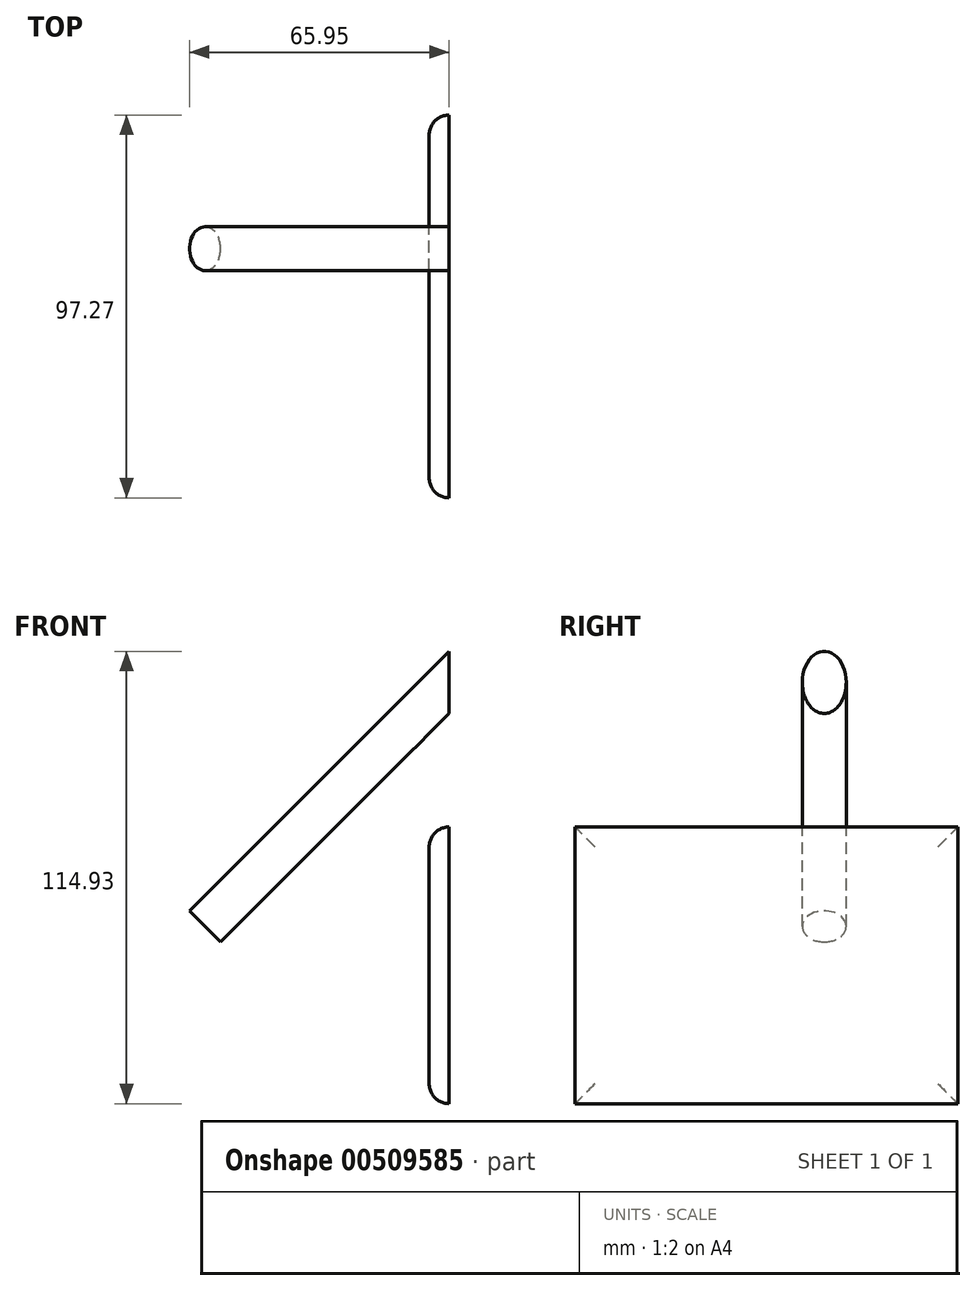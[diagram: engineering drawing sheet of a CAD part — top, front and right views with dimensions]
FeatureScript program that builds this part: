
annotation { "Feature Type Name" : "Feature", "Feature Type Description" : "" }
export const myFeature = defineFeature(function(context is Context, id is Id, definition is map)
    precondition{}
    {
        {
            var Q0;
            Q0=qCreatedBy(makeId("Right.planeOp"),FACE);
            var sketch = newSketch(context, id + "F0", { "sketchPlane" : qUnion([Q0])});
            skLineSegment(sketch, "E0.bottom", {"start": v(-42.41, 32.52) * mm, "end": v(54.86, 32.52) * mm});
            skLineSegment(sketch, "E0.top", {"start": v(-42.41, -37.79) * mm, "end": v(54.86, -37.79) * mm});
            skLineSegment(sketch, "E0.left", {"start": v(-42.41, 32.52) * mm, "end": v(-42.41, -37.79) * mm});
            skLineSegment(sketch, "E0.right", {"start": v(54.86, 32.52) * mm, "end": v(54.86, -37.79) * mm});
            skSolve(sketch);
        }
        {
            var Q0;
            Q0=makeQuery(id+"F0.imprint","IMPRINT",FACE,{"disambiguationData":[TD([[makeQuery(id+"F0.imprint","IMPRINT",EDGE,{"derivedFrom":sQuery(id+"F0.wireOp",EDGE,"E0.bottom")}),-1.0]])]});
            extrude(context, id + "F1", {"entities" : qUnion([Q0]), "oppositeDirection" : true, "depth" : 5.08 * mm});
        }
        {
            var Q0;
            Q0=makeQuery(id+"F1.opExtrude","CAP_FACE",FACE,{"disambiguationData":[OSD([sQuery(id+"F0.wireOp",EDGE,"E0.bottom"),sQuery(id+"F0.wireOp",EDGE,"E0.top"),sQuery(id+"F0.wireOp",EDGE,"E0.left"),sQuery(id+"F0.wireOp",EDGE,"E0.right")])],"isStart":false});
            fillet(context, id + "F2", {"entities" : qUnion([Q0]), "radius" : 5.08 * mm, "tangentPropagation" : true, "allowEdgeOverflow" : false});
        }
        {
            var Q0;
            Q0=sQuery(id+"F0.wireOp",EDGE,"E0.top");
            cPlane(context, id + "F3", {"entities" : qUnion([Q0]), "cplaneType" : CPlaneType.LINE_ANGLE, "offset" : 25.4 * mm, "angle" : 45 * degree, "width" : 152.4 * mm, "height" : 152.4 * mm});
        }
        {
            var Q0;
            Q0=qCreatedBy(id+"F3.planeOp",FACE);
            var sketch = newSketch(context, id + "F4", { "sketchPlane" : qUnion([Q0])});
            skCircle(sketch, "E1", {"center": v(20.9, 48.96) * mm, "radius": 5.58 * mm});
            skSolve(sketch);
        }
        {
            var Q0;
            Q0=makeQuery(id+"F4.imprint","IMPRINT",FACE,{"disambiguationData":[TD([[makeQuery(id+"F4.imprint","IMPRINT",EDGE,{"derivedFrom":sQuery(id+"F4.wireOp",EDGE,"E1")}),1.0]])]});
            extrude(context, id + "F5", {"entities" : qUnion([Q0]), "operationType" : NewBodyOperationType.ADD, "oppositeDirection" : true, "depth" : 12 * mm});
        }
        {
            var Q0;
            Q0=makeQuery(id+"F5.opExtrude","CAP_FACE",FACE,{"disambiguationData":[OSD([sQuery(id+"F4.wireOp",EDGE,"E1")])],"isStart":true});
            var Q1;
            Q1=makeQuery(id+"F1.opExtrude","CAP_FACE",FACE,{"disambiguationData":[OSD([sQuery(id+"F0.wireOp",EDGE,"E0.bottom"),sQuery(id+"F0.wireOp",EDGE,"E0.top"),sQuery(id+"F0.wireOp",EDGE,"E0.left"),sQuery(id+"F0.wireOp",EDGE,"E0.right")])],"isStart":true});
            extrude(context, id + "F6", {"entities" : qUnion([Q0]), "operationType" : NewBodyOperationType.ADD, "endBound" : BoundingType.UP_TO_SURFACE, "endBoundEntityFace" : qUnion([Q1]), "depth" : 25.4 * mm});
        }
    });
